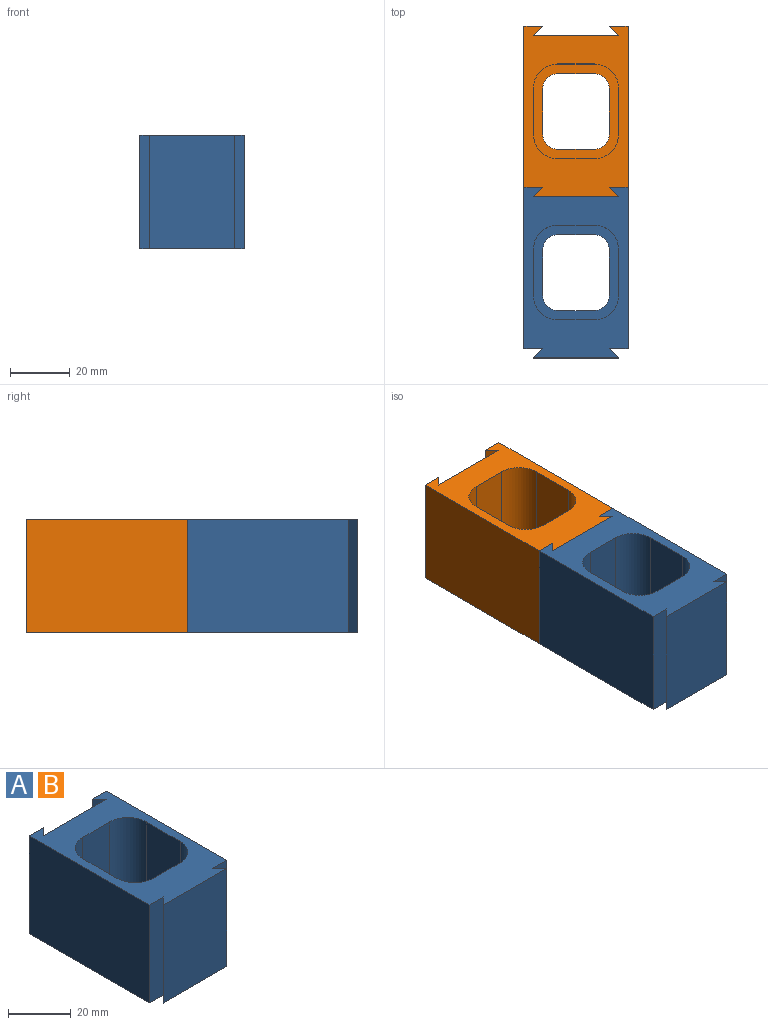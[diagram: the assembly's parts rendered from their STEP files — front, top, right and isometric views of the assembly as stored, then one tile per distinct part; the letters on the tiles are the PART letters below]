
ASSEMBLY  parts=2 mates=1
PART A: 31 faces, bbox 34.9x57.2x38.1 mm
  f0: plane 31.75x28.58mm, normal (0,0,1), area 306.4mm2, adj f8,f9,f10,f11,f12,f13,f14,f15
  f1: plane 57.15x34.93mm, normal (0,0,-1), area 1342.7mm2, adj f3,f4,f5,f6,f7,f16,f17,f18
  f2: plane 57.15x34.93mm, normal (0,0,1), area 1036.3mm2, adj f3,f4,f5,f6,f7,f8,f9,f10
  f3: plane 38.1x6.35mm, normal (0,1,0), area 241.9mm2, adj f1,f2,f6,f21
  f4: plane 38.1x6.35mm, normal (0,-1,0), area 241.9mm2, adj f1,f2,f5,f18
  f5: plane 53.98x38.1mm, normal (1,0,0), area 2056.4mm2, adj f1,f2,f4,f19
  f6: plane 53.98x38.1mm, normal (-1,0,0), area 2056.4mm2, adj f1,f2,f3,f7
  f7: plane 38.1x6.35mm, normal (0,-1,0), area 241.9mm2, adj f1,f2,f6,f17
  f8: plane 34.93x15.24mm, normal (-1,0,0), area 532.3mm2, adj f0,f2,f12,f15
  f9: plane 34.93x12.07mm, normal (0,-1,0), area 421.4mm2, adj f0,f2,f12,f13
  f10: plane 34.93x15.24mm, normal (1,0,0), area 532.3mm2, adj f0,f2,f13,f14
  f11: plane 34.93x12.07mm, normal (0,1,0), area 421.4mm2, adj f0,f2,f14,f15
  f12: cylinder r=8.26mm len=34.93mm, axis (0,0,1), area 452.9mm2, adj f0,f2,f8,f9
  f13: cylinder r=8.26mm len=34.93mm, axis (0,0,-1), area 452.9mm2, adj f0,f2,f9,f10
  f14: cylinder r=8.26mm len=34.93mm, axis (0,0,1), area 452.9mm2, adj f0,f2,f10,f11
  f15: cylinder r=8.26mm len=34.93mm, axis (0,0,-1), area 452.9mm2, adj f0,f2,f8,f11
  f16: plane 38.1x28.58mm, normal (0,-1,0), area 1088.7mm2, adj f1,f2,f17,f18
  f17: plane 38.1x3.18mm, normal (-0.71,0.71,0), area 171.1mm2, adj f1,f2,f7,f16
  f18: plane 38.1x3.18mm, normal (0.71,0.71,0), area 171.1mm2, adj f1,f2,f4,f16
  f19: plane 38.1x6.35mm, normal (0,1,0), area 241.9mm2, adj f1,f2,f5,f20
  f20: plane 38.1x3.18mm, normal (-0.71,-0.71,0), area 171.1mm2, adj f1,f2,f19,f22
  f21: plane 38.1x3.18mm, normal (0.71,-0.71,0), area 171.1mm2, adj f1,f2,f3,f22
  f22: plane 38.1x28.58mm, normal (0,1,0), area 1088.7mm2, adj f1,f2,f20,f21
  f23: plane 15.24x3.18mm, normal (-1,0,0), area 48.4mm2, adj f0,f1,f27,f30
  f24: plane 12.07x3.18mm, normal (0,-1,0), area 38.3mm2, adj f0,f1,f27,f28
  f25: plane 15.24x3.18mm, normal (1,0,0), area 48.4mm2, adj f0,f1,f28,f29
  f26: plane 12.07x3.18mm, normal (0,1,0), area 38.3mm2, adj f0,f1,f29,f30
  f27: cylinder r=5.08mm len=5.08mm, axis (0,0,1), area 25.3mm2, adj f0,f1,f23,f24
  f28: cylinder r=5.08mm len=5.08mm, axis (0,0,-1), area 25.3mm2, adj f0,f1,f24,f25
  f29: cylinder r=5.08mm len=5.08mm, axis (0,0,1), area 25.3mm2, adj f0,f1,f25,f26
  f30: cylinder r=5.08mm len=5.08mm, axis (0,0,-1), area 25.3mm2, adj f0,f1,f23,f26
PART B: same geometry as A
PLACE A t=(26.41,-17.46,15.91)mm
PLACE B t=(26.41,36.51,15.91)mm
MATE fastened A.f22 <-> B.f16  axis (0,1,0) through (26.41,7.94,34.96)mm
